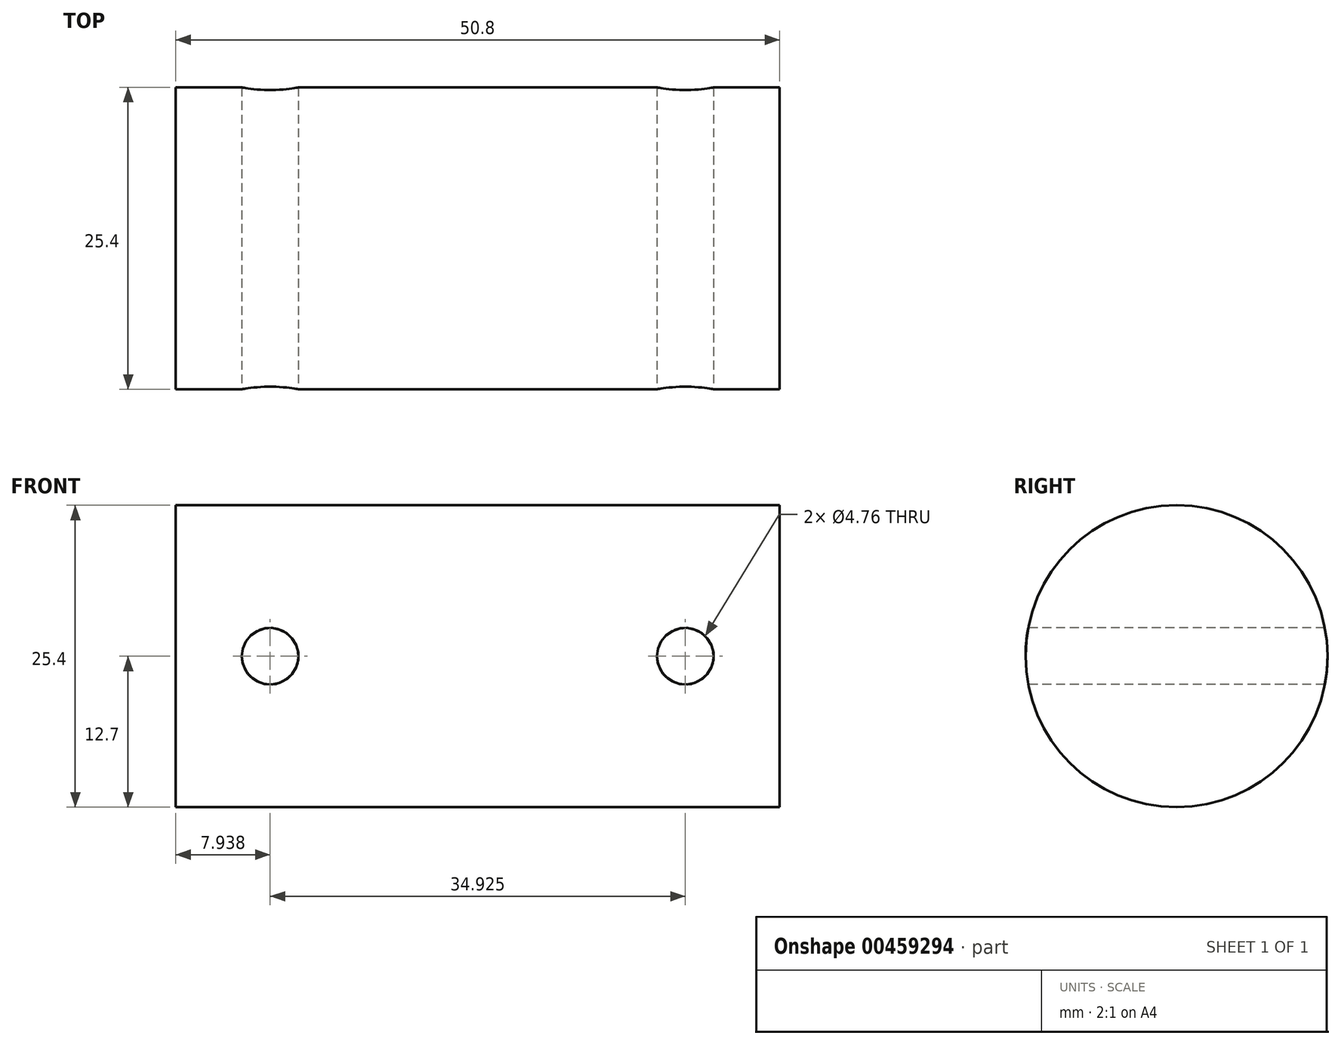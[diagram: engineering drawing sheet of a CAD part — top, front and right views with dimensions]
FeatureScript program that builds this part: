
annotation { "Feature Type Name" : "Feature", "Feature Type Description" : "" }
export const myFeature = defineFeature(function(context is Context, id is Id, definition is map)
    precondition{}
    {
        {
            var Q0;
            Q0=qCreatedBy(makeId("Front.planeOp"),FACE);
            var sketch = newSketch(context, id + "F0", { "sketchPlane" : qUnion([Q0])});
            skLineSegment(sketch, "E0", {"start": v(0, 0) * mm, "end": v(50.8, 0) * mm});
            skLineSegment(sketch, "E1", {"start": v(50.8, 0) * mm, "end": v(50.8, 12.7) * mm});
            skLineSegment(sketch, "E2", {"start": v(50.8, 12.7) * mm, "end": v(0, 12.7) * mm});
            skLineSegment(sketch, "E3", {"start": v(0, 12.7) * mm, "end": v(0, 0) * mm});
            skLineSegment(sketch, "E4.bottom", {"start": v(0, 12.7) * mm, "end": v(50.8, 12.7) * mm});
            skLineSegment(sketch, "E4.top", {"start": v(0, -12.7) * mm, "end": v(50.8, -12.7) * mm});
            skLineSegment(sketch, "E4.left", {"start": v(0, 12.7) * mm, "end": v(0, -12.7) * mm});
            skLineSegment(sketch, "E4.right", {"start": v(50.8, 12.7) * mm, "end": v(50.8, -12.7) * mm});
            skLineSegment(sketch, "E5", {"start": v(7.94, 12.7) * mm, "end": v(7.94, -12.7) * mm});
            skLineSegment(sketch, "E6", {"start": v(42.86, 12.7) * mm, "end": v(42.86, -12.7) * mm});
            skSolve(sketch);
        }
        {
            var Q0;
            {var subQ0=sQuery(id+"F0.wireOp",EDGE,"E0");Q0=makeQuery(id+"F0.imprint","IMPRINT",FACE,{"disambiguationData":[TD([[makeQuery(id+"F0.imprint","IMPRINT",EDGE,{"derivedFrom":subQ0}),-1.0]])]});}
            var Q1;
            {var subQ0=sQuery(id+"F0.wireOp",EDGE,"E0");Q1=makeQuery(id+"F0.imprint","IMPRINT",FACE,{"disambiguationData":[TD([[makeQuery(id+"F0.imprint","IMPRINT",EDGE,{"derivedFrom":subQ0}),1.0]])]});}
            extrude(context, id + "F1", {"entities" : qUnion([Q0, Q1]), "endBound" : BoundingType.SYMMETRIC, "depth" : 25.4 * mm});
        }
        {
            var Q0;
            Q0=makeQuery(id+"F1.opExtrude","CAP_FACE",FACE,{"disambiguationData":[OSD([sQuery(id+"F0.wireOp",EDGE,"E4.bottom"),sQuery(id+"F0.wireOp",EDGE,"E4.top"),sQuery(id+"F0.wireOp",EDGE,"E4.left"),sQuery(id+"F0.wireOp",EDGE,"E4.right")])],"isStart":false});
            var sketch = newSketch(context, id + "F2", { "sketchPlane" : qUnion([Q0])});
            skLineSegment(sketch, "E7", {"start": v(7.94, 12.7) * mm, "end": v(7.94, -12.7) * mm});
            skLineSegment(sketch, "E8", {"start": v(42.86, 12.7) * mm, "end": v(42.86, -12.7) * mm});
            skCircle(sketch, "E9", {"center": v(7.94, 0) * mm, "radius": 2.38 * mm});
            skCircle(sketch, "E10", {"center": v(42.86, 0) * mm, "radius": 2.38 * mm});
            skSolve(sketch);
        }
        {
            var Q0;
            Q0=sQuery(id+"F2.wireOp",VERTEX,"E9.center");
            var Q1;
            Q1=sQuery(id+"F2.wireOp",VERTEX,"E10.center");
            var Q2;
            Q2=makeQuery(id+"F1.opExtrude","SWEPT_BODY",BODY,{"disambiguationData":[OSD([sQuery(id+"F0.wireOp",EDGE,"E4.bottom"),sQuery(id+"F0.wireOp",EDGE,"E4.top"),sQuery(id+"F0.wireOp",EDGE,"E4.left"),sQuery(id+"F0.wireOp",EDGE,"E4.right")])]});
            hole(context, id + "F3", {"style" : HoleStyle.SIMPLE, "endStyle" : HoleEndStyle.THROUGH, "holeDiameter" : 4.76 * mm, "isTappedThrough" : true, "tappedDepth" : 7.14 * mm, "tapClearance" : 3, "startFromSketch" : true, "locations" : qUnion([Q0, Q1]), "scope" : qUnion([Q2])});
        }
        {
            var Q0;
            Q0=makeQuery(id+"F1.opExtrude","SWEPT_FACE",FACE,{"disambiguationData":[OSD([sQuery(id+"F0.wireOp",EDGE,"E4.left")])]});
            var sketch = newSketch(context, id + "F4", { "sketchPlane" : qUnion([Q0])});
            skCircle(sketch, "E11", {"center": v(0, 0) * mm, "radius": 12.7 * mm});
            skSolve(sketch);
        }
        {
            var Q0;
            {var subQ0=sQuery(id+"F4.wireOp",EDGE,"E11");var subQ1=sQuery(id+"F0.wireOp",EDGE,"E4.left");var subQ4=makeQuery(id+"F1.opExtrude","CAP_EDGE",EDGE,{"disambiguationData":[OSD([subQ1])],"isStart":false});var subQ5=makeQuery(id+"F4.imprint","INTERSECT",VERTEX,{"derivedFrom":[subQ4,subQ0]});Q0=makeQuery(id+"F4.imprint","IMPRINT",FACE,{"disambiguationData":[TD([[makeQuery(id+"F4.imprint","IMPRINT",EDGE,{"disambiguationData":[TD([[subQ5,-1.0]])],"derivedFrom":subQ0}),-1.0]])]});}
            var Q1;
            {var subQ0=sQuery(id+"F4.wireOp",EDGE,"E11");var subQ1=sQuery(id+"F0.wireOp",EDGE,"E4.left");var subQ4=makeQuery(id+"F1.opExtrude","CAP_EDGE",EDGE,{"disambiguationData":[OSD([subQ1])],"isStart":true});var subQ5=makeQuery(id+"F4.imprint","INTERSECT",VERTEX,{"derivedFrom":[subQ4,subQ0]});Q1=makeQuery(id+"F4.imprint","IMPRINT",FACE,{"disambiguationData":[TD([[makeQuery(id+"F4.imprint","IMPRINT",EDGE,{"disambiguationData":[TD([[subQ5,1.0]])],"derivedFrom":subQ0}),-1.0]])]});}
            var Q2;
            {var subQ0=sQuery(id+"F4.wireOp",EDGE,"E11");var subQ1=sQuery(id+"F0.wireOp",EDGE,"E4.left");var subQ2=makeQuery(id+"F1.opExtrude","CAP_EDGE",EDGE,{"disambiguationData":[OSD([subQ1])],"isStart":true});var subQ3=makeQuery(id+"F4.imprint","INTERSECT",VERTEX,{"derivedFrom":[subQ2,subQ0]});Q2=makeQuery(id+"F4.imprint","IMPRINT",FACE,{"disambiguationData":[TD([[makeQuery(id+"F4.imprint","IMPRINT",EDGE,{"disambiguationData":[TD([[subQ3,-1.0]])],"derivedFrom":subQ0}),-1.0]])]});}
            var Q3;
            {var subQ0=sQuery(id+"F4.wireOp",EDGE,"E11");var subQ1=sQuery(id+"F0.wireOp",EDGE,"E4.left");var subQ2=makeQuery(id+"F1.opExtrude","CAP_EDGE",EDGE,{"disambiguationData":[OSD([subQ1])],"isStart":false});var subQ3=makeQuery(id+"F4.imprint","INTERSECT",VERTEX,{"derivedFrom":[subQ2,subQ0]});Q3=makeQuery(id+"F4.imprint","IMPRINT",FACE,{"disambiguationData":[TD([[makeQuery(id+"F4.imprint","IMPRINT",EDGE,{"disambiguationData":[TD([[subQ3,1.0]])],"derivedFrom":subQ0}),-1.0]])]});}
            extrude(context, id + "F5", {"entities" : qUnion([Q0, Q1, Q2, Q3]), "operationType" : NewBodyOperationType.REMOVE, "oppositeDirection" : true, "depth" : 50.8 * mm});
        }
    });
